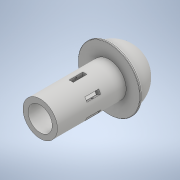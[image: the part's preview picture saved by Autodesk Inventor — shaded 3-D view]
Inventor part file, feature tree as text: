
AUTODESK INVENTOR PART (.ipt)
format: ipt  version: 2020 (Build 240168000, 168)  size: 327,680 bytes
history: native  units: mm
features: sketch x9, other x5, extrude x4, projected_geometry x4, pattern_circular x3, fillet x2, plane x1
ambient origin geometry x8: Origin, YZ Plane, XZ Plane, XY Plane, X Axis, Y Axis, Z Axis, Center Point
bodies: Body1 (feature_tree)
feature tree (28):
  other  "實體1"
  other  "迴轉1"
  other  "迴轉2"
  fillet  "圓角1"  Radius=100.0mm
  fillet  "圓角2"  Radius=25.0mm
  other  "迴轉3"
  extrude  "擠出1"  TaperAngle=90.0deg  [1 undecoded]
  extrude  "擠出2"  Depth=5.0mm
  pattern_circular  "環形陣列1"  [2 undecoded]
  other  "迴轉4"
  extrude  "擠出4"  TaperAngle=90.0deg  [1 undecoded]
  pattern_circular  "環形陣列2"  [2 undecoded]
  sketch  "草圖9"
  plane  "工作平面1"
  extrude  "擠出5"  Depth=0.5mm
  pattern_circular  "環形陣列3"  Angle=90.0deg  [1 undecoded]
  sketch  "草圖1"
  sketch  "草圖2"
  sketch  "草圖3"
  sketch  "草圖4"
  sketch  "草圖5"
  projected_geometry  "投影迴路1"
  sketch  "草圖7"
  sketch  "草圖8"
  projected_geometry  "投影迴路2"
  projected_geometry  "投影迴路3"
  sketch  "草圖10"
  projected_geometry  "投影迴路4"
note: 7 required parameter values undecoded (feature->parameter linkage not recoverable at this tier; creation-order binding heuristic only, values carry confidence <= 0.55)
